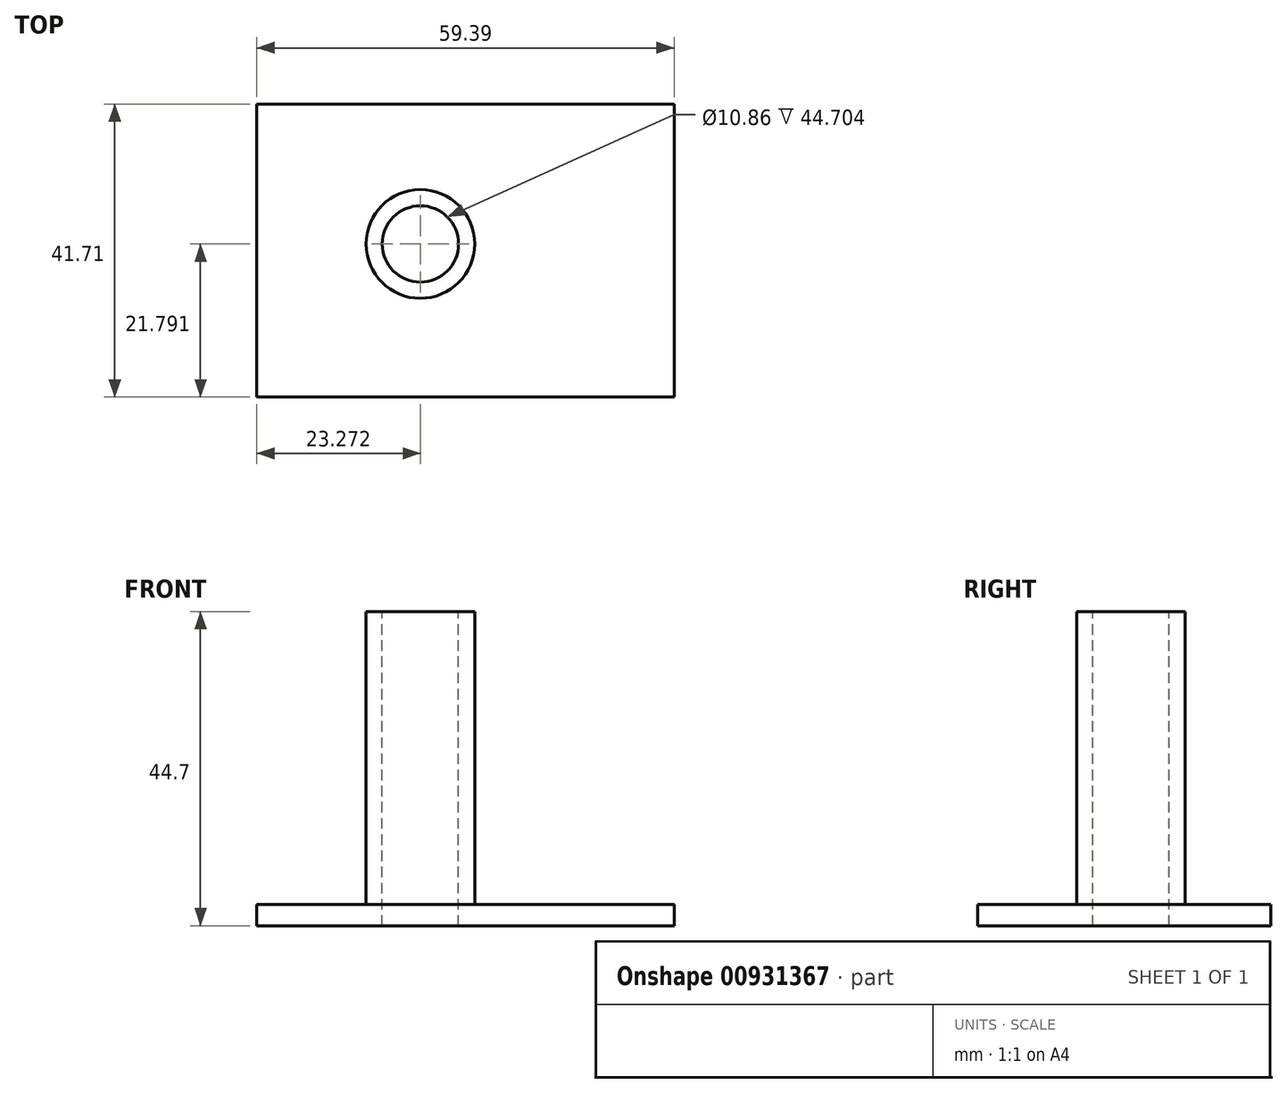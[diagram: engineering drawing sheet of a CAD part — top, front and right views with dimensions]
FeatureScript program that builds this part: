
annotation { "Feature Type Name" : "Feature", "Feature Type Description" : "" }
export const myFeature = defineFeature(function(context is Context, id is Id, definition is map)
    precondition{}
    {
        {
            var Q0;
            Q0=qCreatedBy(makeId("Top.planeOp"),FACE);
            var sketch = newSketch(context, id + "F0", { "sketchPlane" : qUnion([Q0])});
            skLineSegment(sketch, "E0.bottom", {"start": v(0, 0) * mm, "end": v(59.4, 0) * mm});
            skLineSegment(sketch, "E0.top", {"start": v(0, -41.7) * mm, "end": v(59.4, -41.7) * mm});
            skLineSegment(sketch, "E0.left", {"start": v(0, 0) * mm, "end": v(0, -41.7) * mm});
            skLineSegment(sketch, "E0.right", {"start": v(59.4, 0) * mm, "end": v(59.4, -41.7) * mm});
            skSolve(sketch);
        }
        {
            var Q0;
            Q0 = qSketchRegion(id + "F0", true);
            extrude(context, id + "F1", {"entities" : qUnion([Q0]), "depth" : 3.05 * mm, "offsetDistance" : 25.4 * mm});
        }
        {
            var Q0;
            Q0=makeQuery(id+"F1.opExtrude","CAP_FACE",FACE,{"disambiguationData":[OSD([sQuery(id+"F0.wireOp",EDGE,"E0.bottom"),sQuery(id+"F0.wireOp",EDGE,"E0.top"),sQuery(id+"F0.wireOp",EDGE,"E0.left"),sQuery(id+"F0.wireOp",EDGE,"E0.right")])],"isStart":false});
            var sketch = newSketch(context, id + "F2", { "sketchPlane" : qUnion([Q0])});
            skCircle(sketch, "E1", {"center": v(23.27, -19.92) * mm, "radius": 7.74 * mm});
            skSolve(sketch);
        }
        {
            var Q0;
            Q0 = qSketchRegion(id + "F2", true);
            extrude(context, id + "F3", {"entities" : qUnion([Q0]), "operationType" : NewBodyOperationType.ADD, "depth" : 41.66 * mm, "offsetDistance" : 25.4 * mm});
        }
        {
            var Q0;
            Q0=makeQuery(id+"F3.opExtrude","CAP_FACE",FACE,{"disambiguationData":[OSD([sQuery(id+"F2.wireOp",EDGE,"E1")])],"isStart":false});
            var sketch = newSketch(context, id + "F4", { "sketchPlane" : qUnion([Q0])});
            skCircle(sketch, "E2", {"center": v(23.27, -19.92) * mm, "radius": 5.43 * mm});
            skSolve(sketch);
        }
        {
            var Q0;
            Q0=makeQuery(id+"F4.imprint","IMPRINT",FACE,{"disambiguationData":[TD([[makeQuery(id+"F4.imprint","IMPRINT",EDGE,{"derivedFrom":sQuery(id+"F4.wireOp",EDGE,"E2")}),1.0]])]});
            extrude(context, id + "F5", {"entities" : qUnion([Q0]), "operationType" : NewBodyOperationType.REMOVE, "oppositeDirection" : true, "depth" : 50.8 * mm, "offsetDistance" : 25.4 * mm});
        }
    });
